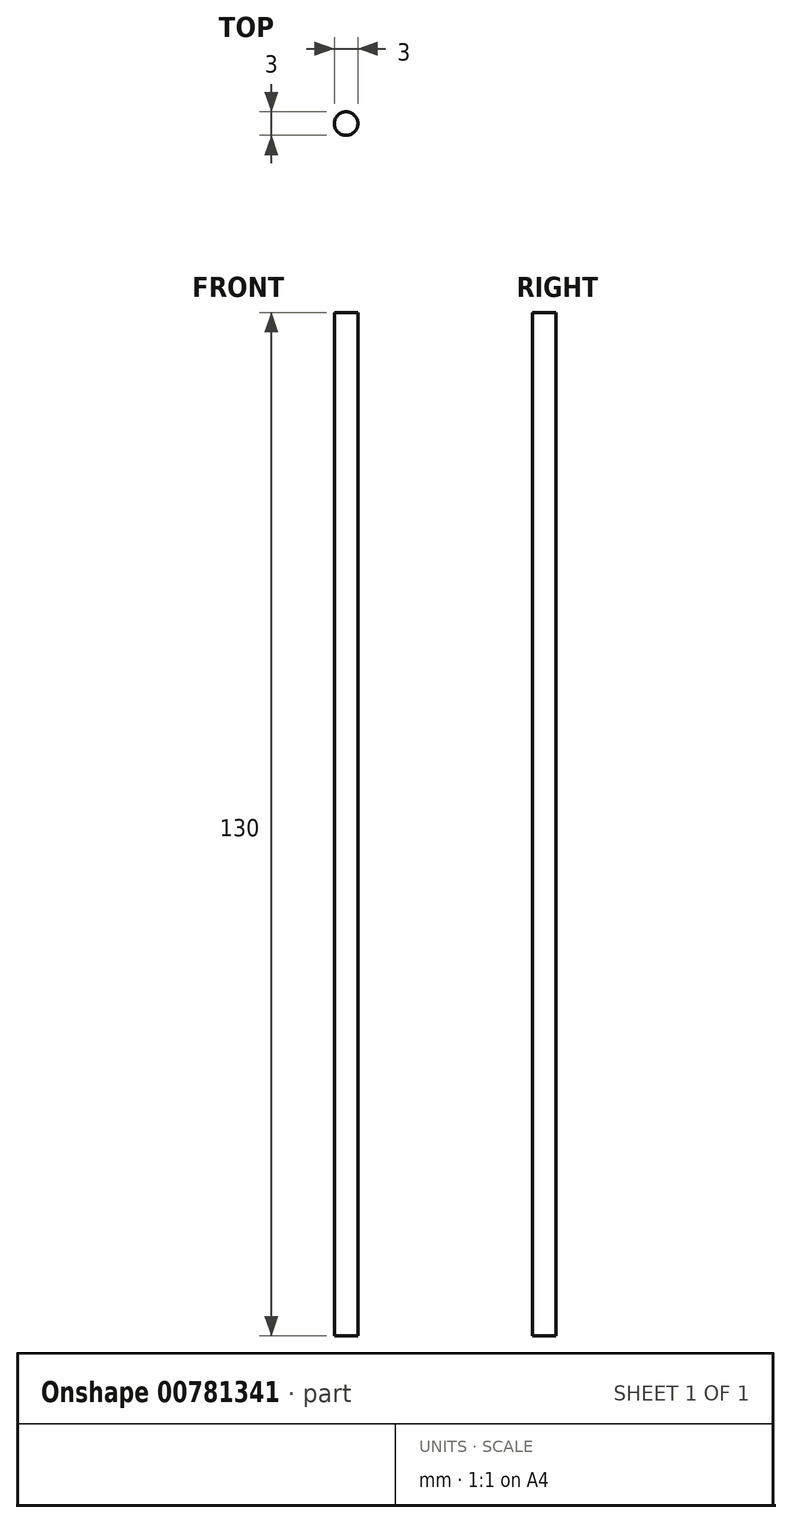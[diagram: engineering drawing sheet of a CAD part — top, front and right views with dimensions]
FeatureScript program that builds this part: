
annotation { "Feature Type Name" : "Feature", "Feature Type Description" : "" }
export const myFeature = defineFeature(function(context is Context, id is Id, definition is map)
    precondition{}
    {
        {
            var Q0;
            Q0=qCreatedBy(makeId("Top.planeOp"),FACE);
            var sketch = newSketch(context, id + "F0", { "sketchPlane" : qUnion([Q0])});
            skCircle(sketch, "E0", {"center": v(0, 0) * mm, "radius": 1.5 * mm});
            skSolve(sketch);
        }
        {
            var Q0;
            Q0 = qSketchRegion(id + "F0", true);
            extrude(context, id + "F1", {"entities" : qUnion([Q0]), "endBound" : BoundingType.SYMMETRIC, "depth" : 130 * mm, "offsetDistance" : 25 * mm});
        }
    });
